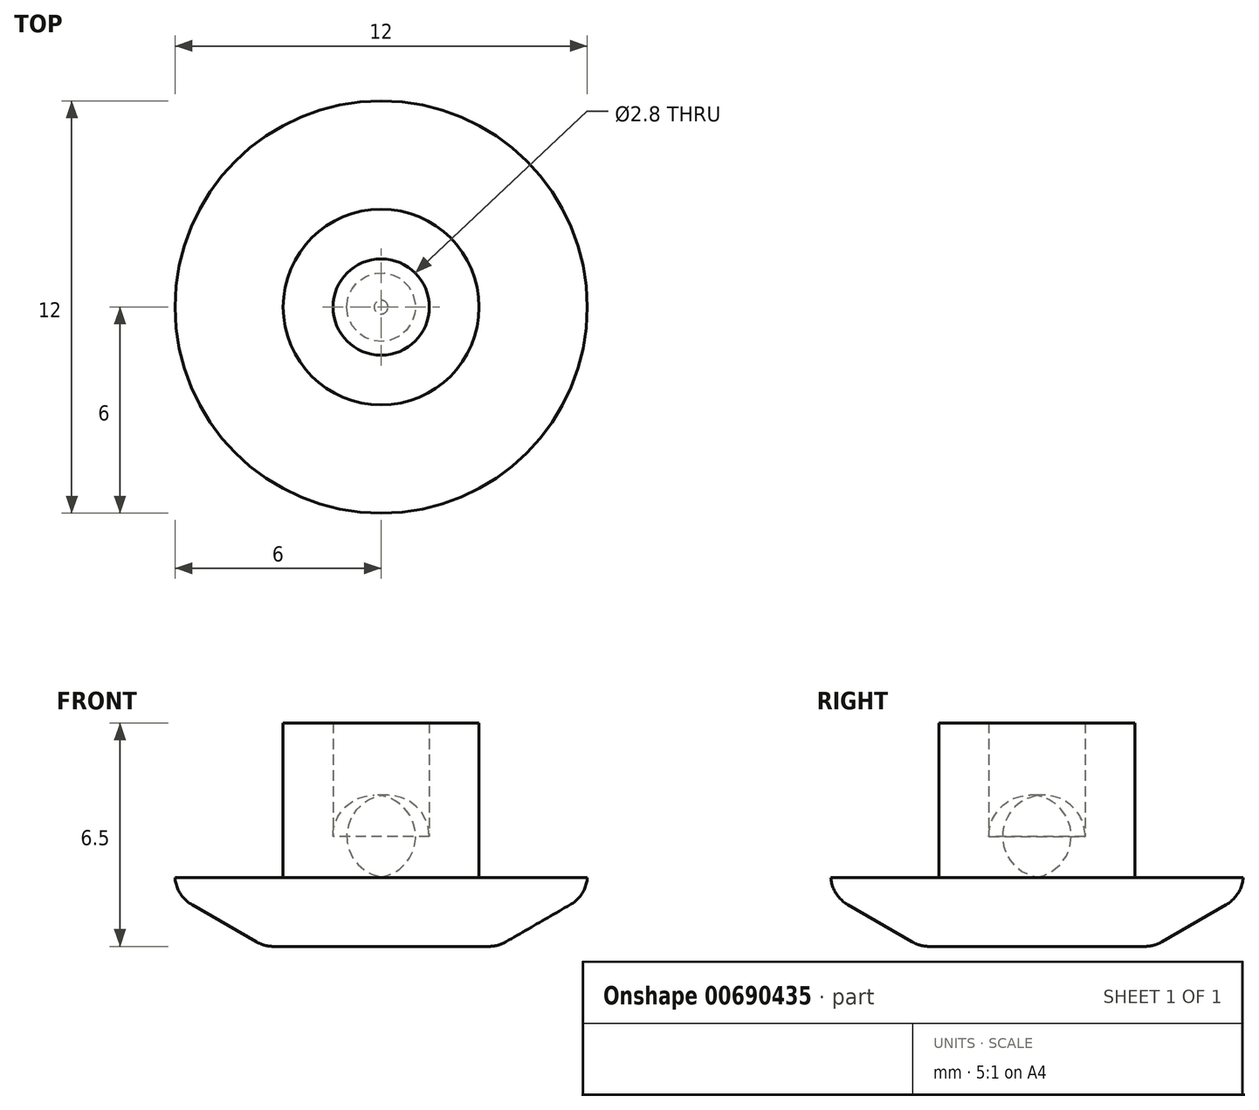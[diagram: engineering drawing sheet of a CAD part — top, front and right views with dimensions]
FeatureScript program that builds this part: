
annotation { "Feature Type Name" : "Feature", "Feature Type Description" : "" }
export const myFeature = defineFeature(function(context is Context, id is Id, definition is map)
    precondition{}
    {
        {
            var Q0;
            Q0=qCreatedBy(makeId("Top.planeOp"),FACE);
            var sketch = newSketch(context, id + "F0", { "sketchPlane" : qUnion([Q0])});
            skCircle(sketch, "E0", {"center": v(0, 0) * mm, "radius": 6 * mm});
            skSolve(sketch);
        }
        {
            var Q0;
            Q0=qSketchRegion(id+"F0",true);
            extrude(context, id + "F1", {"entities" : qUnion([Q0]), "depth" : 2 * mm, "offsetDistance" : 25 * mm});
        }
        {
            var Q0;
            Q0=makeQuery(id+"F1.opExtrude","CAP_EDGE",EDGE,{"disambiguationData":[OSD([sQuery(id+"F0.wireOp",EDGE,"E0")])],"isStart":true});
            chamfer(context, id + "F2", {"entities" : qUnion([Q0]), "chamferType" : ChamferType.OFFSET_ANGLE, "width" : 1.5 * mm, "oppositeDirection" : false, "angle" : 60 * degree, "tangentPropagation" : true});
        }
        {
            var Q0;
            {var subQ0=sQuery(id+"F0.wireOp",EDGE,"E0");Q0=makeQuery(id+"F2.opChamfer","BLEND_EDGE",EDGE,{"blendedFrom":[makeQuery(id+"F1.opExtrude","CAP_EDGE",EDGE,{"disambiguationData":[OSD([subQ0])],"isStart":true}),makeQuery(id+"F1.opExtrude","CAP_FACE",FACE,{"disambiguationData":[OSD([subQ0])],"isStart":true})],"blendedInto":[makeQuery(id+"F1.opExtrude","CAP_FACE",FACE,{"disambiguationData":[OSD([subQ0])],"isStart":true})]});}
            var Q1;
            {var subQ0=sQuery(id+"F0.wireOp",EDGE,"E0");Q1=makeQuery(id+"F2.opChamfer","BLEND_EDGE",EDGE,{"blendedFrom":[makeQuery(id+"F1.opExtrude","CAP_EDGE",EDGE,{"disambiguationData":[OSD([subQ0])],"isStart":true}),makeQuery(id+"F1.opExtrude","SWEPT_FACE",FACE,{"disambiguationData":[OSD([subQ0])]})],"blendedInto":[makeQuery(id+"F1.opExtrude","SWEPT_FACE",FACE,{"disambiguationData":[OSD([subQ0])]})]});}
            fillet(context, id + "F3", {"entities" : qUnion([Q0, Q1]), "radius" : 1 * mm, "tangentPropagation" : true, "allowEdgeOverflow" : false});
        }
        {
            var Q0;
            Q0=makeQuery(id+"F1.opExtrude","CAP_FACE",FACE,{"disambiguationData":[OSD([sQuery(id+"F0.wireOp",EDGE,"E0")])],"isStart":false});
            var sketch = newSketch(context, id + "F4", { "sketchPlane" : qUnion([Q0])});
            skCircle(sketch, "E1", {"center": v(0, 0) * mm, "radius": 2.85 * mm});
            skCircle(sketch, "E2", {"center": v(0, 0) * mm, "radius": 1.4 * mm});
            skSolve(sketch);
        }
        {
            var Q0;
            Q0=qSketchRegion(id+"F4",true);
            extrude(context, id + "F5", {"entities" : qUnion([Q0]), "operationType" : NewBodyOperationType.ADD, "depth" : 4.5 * mm, "offsetDistance" : 25 * mm});
        }
        {
            var Q0;
            Q0=makeQuery(id+"F5.opExtrude","CAP_EDGE",EDGE,{"disambiguationData":[OSD([sQuery(id+"F4.wireOp",EDGE,"E2")])],"isStart":true});
            fillet(context, id + "F6", {"entities" : qUnion([Q0]), "radius" : 1.2 * mm, "tangentPropagation" : true, "allowEdgeOverflow" : false});
        }
    });
